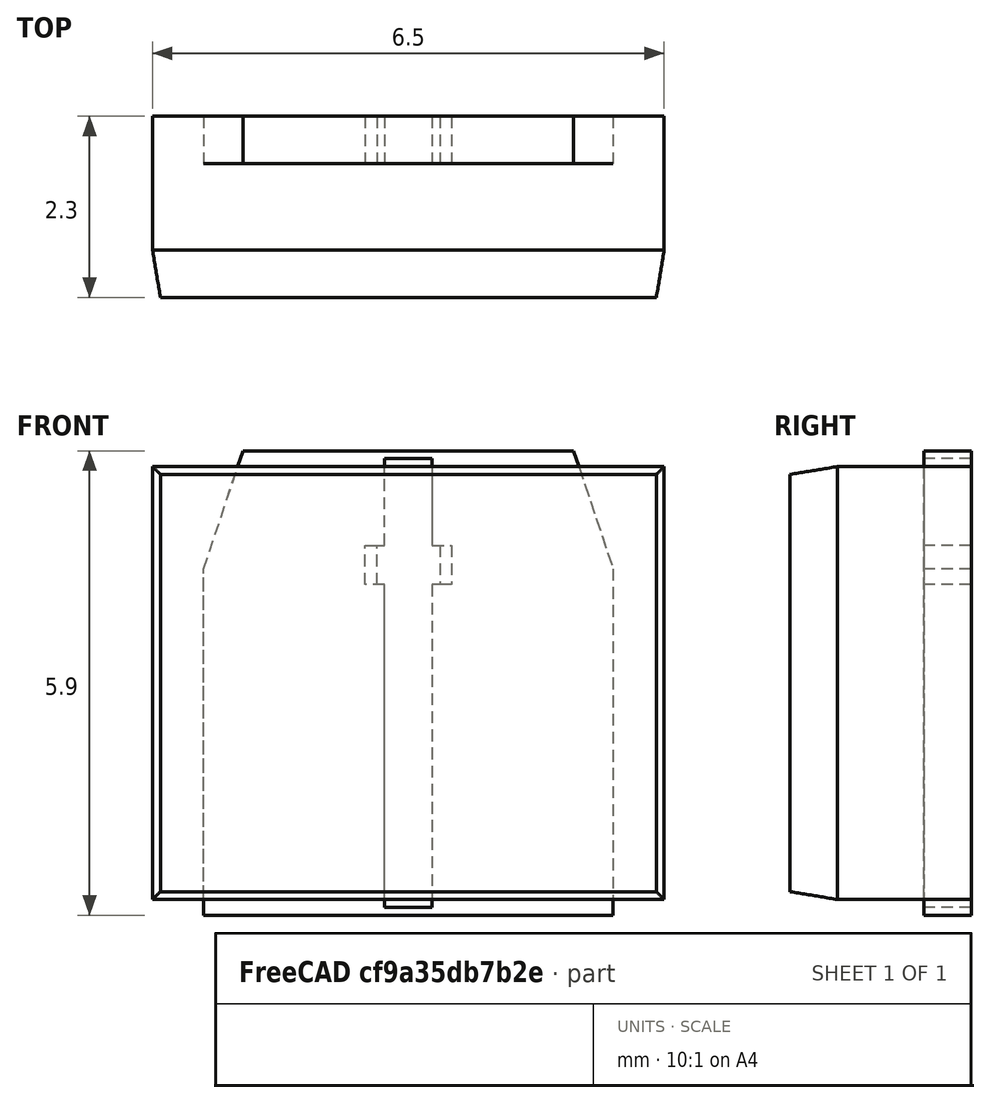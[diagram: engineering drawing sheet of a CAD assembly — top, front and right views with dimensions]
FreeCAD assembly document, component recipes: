
FREECAD ASSEMBLY — COMPONENT RECIPES ("2SK4017_3Dmodel")

This assembly document has 4 components, labeled P0..P3 below (a component is one placed body or linked part). 4 of them carry a construction recipe — the FreeCAD feature program that regenerates the part from scratch, quoted from this document or its linked companion documents; the rest are supplied as boundary geometry only. No exploded tour is included for this assembly.
COMPONENT P0 — recipe-attached ("樹脂体", modeled in this document).
Construction recipe (the document's own serialized feature program — sketch geometry with constraints, then the solid features built on it; lengths are millimeters unless a unit is written):

FEATURE [Sketcher::SketchObject] Sketch
  FullyConstrained = true
  MapMode = 5
  Placement = pos=(0,0,0) rot=(1,0,0;1.5708rad)
  Support = -> [XZ_Plane]
  sketch-geometry (4):
    g0: LineSegment StartX=-3.25 StartY=2.75 StartZ=0 EndX=3.25 EndY=2.75 EndZ=0
    g1: LineSegment StartX=3.25 StartY=2.75 StartZ=0 EndX=3.25 EndY=-2.75 EndZ=0
    g2: LineSegment StartX=3.25 StartY=-2.75 StartZ=0 EndX=-3.25 EndY=-2.75 EndZ=0
    g3: LineSegment StartX=-3.25 StartY=-2.75 StartZ=0 EndX=-3.25 EndY=2.75 EndZ=0
  constraints (11):
    c: Coincident(g0,g1)
    c: Coincident(g1,g2)
    c: Coincident(g2,g3)
    c: Coincident(g3,g0)
    c: Horizontal(g0)
    c: Horizontal(g2)
    c: Vertical(g1)
    c: Vertical(g3)
    c: DistanceX(g0,g0) = 6.5
    c: DistanceY(g1,g1) = 5.5
    c: Symmetric(g1,g0,g-1)
FEATURE [PartDesign::Pad] Pad
  Direction = (1,1,1)
  Length = 1.7
  Length2 = 100
  Placement = pos=(0,0,0) rot=(1,0,0;1.5708rad)
  Profile = -> Sketch
  Type = 0
FEATURE [Sketcher::SketchObject] Sketch001
  AttachmentOffset = pos=(0,0,0.6) rot=(0,0,1;0rad)
  FullyConstrained = true
  MapMode = 5
  Placement = pos=(0,-2.3,1e-15) rot=(1,0,0;1.5708rad)
  Support = -> [Pad]
  sketch-geometry (4):
    g0: LineSegment StartX=-3.15 StartY=2.65 StartZ=0 EndX=3.15 EndY=2.65 EndZ=0
    g1: LineSegment StartX=3.15 StartY=2.65 StartZ=0 EndX=3.15 EndY=-2.65 EndZ=0
    g2: LineSegment StartX=3.15 StartY=-2.65 StartZ=0 EndX=-3.15 EndY=-2.65 EndZ=0
    g3: LineSegment StartX=-3.15 StartY=-2.65 StartZ=0 EndX=-3.15 EndY=2.65 EndZ=0
  constraints (11):
    c: Coincident(g0,g1)
    c: Coincident(g1,g2)
    c: Coincident(g2,g3)
    c: Coincident(g3,g0)
    c: Horizontal(g0)
    c: Horizontal(g2)
    c: Vertical(g1)
    c: Vertical(g3)
    c: DistanceX(g0,g0) = 6.3
    c: DistanceY(g3,g3) = 5.3
    c: Symmetric(g1,g0,g-1)
FEATURE [Sketcher::SketchObject] Sketch002
  ExternalGeometry = -> [Pad]
  FullyConstrained = true
  MapMode = 5
  Placement = pos=(0,-1.7,8e-16) rot=(1,0,0;1.5708rad)
  Support = -> [Pad]
  sketch-geometry (4):
    g0: LineSegment StartX=-3.25 StartY=2.75 StartZ=0 EndX=3.25 EndY=2.75 EndZ=0
    g1: LineSegment StartX=3.25 StartY=2.75 StartZ=0 EndX=3.25 EndY=-2.75 EndZ=0
    g2: LineSegment StartX=3.25 StartY=-2.75 StartZ=0 EndX=-3.25 EndY=-2.75 EndZ=0
    g3: LineSegment StartX=-3.25 StartY=-2.75 StartZ=0 EndX=-3.25 EndY=2.75 EndZ=0
  constraints (10):
    c: Coincident(g0,g1)
    c: Coincident(g1,g2)
    c: Coincident(g2,g3)
    c: Coincident(g3,g0)
    c: Horizontal(g0)
    c: Horizontal(g2)
    c: Vertical(g1)
    c: Vertical(g3)
    c: Coincident(g1,g-4)
    c: Coincident(g-3,g0)
FEATURE [PartDesign::AdditiveLoft] AdditiveLoft
  BaseFeature = -> Pad
  Closed = false
  Placement = pos=(0,0,0) rot=(1,0,0;1.5708rad)
  Profile = -> Sketch001
  Ruled = false
  Sections = -> [Sketch002]
FEATURE [PartDesign::CoordinateSystem] ______  label="原点"
  AttacherType = Attacher::AttachEngine3D
  MapMode = 1
  Placement = pos=(-3.25,6e-16,2.75) rot=(0,0,1;0rad)
  Support = -> [Pad]
FEATURE [PartDesign::CoordinateSystem] _____________________  label="ドレインリード"
  AttacherType = Attacher::AttachEngine3D
  MapMode = 1
  Placement = pos=(-3.25,-1.7,-2.75) rot=(0,0,1;0rad)
  Support = -> [Pad]
FEATURE [PartDesign::CoordinateSystem] __________________001  label="ソースリード"
  AttacherType = Attacher::AttachEngine3D
  MapMode = 1
  Placement = pos=(-3.25,-1.7,-2.75) rot=(0,0,1;0rad)
  Support = -> [Pad]
FEATURE [PartDesign::CoordinateSystem] __________________002  label="ヒートシンク001"
  AttacherType = Attacher::AttachEngine3D
  AttachmentOffset = pos=(3.25,0,1.5) rot=(0,0,1;0rad)
  MapMode = 1
  Placement = pos=(0,6e-16,4.25) rot=(0,0,1;0rad)
  Support = -> [Pad]
FEATURE [PartDesign::Body] Body  label="樹脂体"
  Group = -> [Sketch,Pad,Sketch001,Sketch002,AdditiveLoft,______,_____________________,__________________001,__________________002]
  Origin = -> Origin
  Tip = -> AdditiveLoft
COMPONENT P1 — recipe-attached ("リードドレイン", modeled in this document).
Construction recipe (the document's own serialized feature program — sketch geometry with constraints, then the solid features built on it; lengths are millimeters unless a unit is written):

FEATURE [Sketcher::SketchObject] Sketch003
  FullyConstrained = true
  MapMode = 5
  Placement = pos=(0,0,0) rot=(1,0,0;1.5708rad)
  Support = -> [XZ_Plane001]
  sketch-geometry (12):
    g0: LineSegment StartX=-0.3 StartY=2.85 StartZ=0 EndX=0.3 EndY=2.85 EndZ=0
    g1: LineSegment StartX=0.3 StartY=2.85 StartZ=0 EndX=0.3 EndY=1.75 EndZ=0
    g2: LineSegment StartX=0.3 StartY=-2.85 StartZ=0 EndX=-0.3 EndY=-2.85 EndZ=0
    g3: LineSegment StartX=-0.3 StartY=-2.85 StartZ=0 EndX=-0.3 EndY=1.25 EndZ=0
    g4: LineSegment StartX=-0.55 StartY=1.75 StartZ=0 EndX=-0.3 EndY=1.75 EndZ=0
    g5: LineSegment StartX=0.55 StartY=1.75 StartZ=0 EndX=0.55 EndY=1.25 EndZ=0
    g6: LineSegment StartX=0.55 StartY=1.25 StartZ=0 EndX=0.3 EndY=1.25 EndZ=0
    g7: LineSegment StartX=-0.55 StartY=1.25 StartZ=0 EndX=-0.55 EndY=1.75 EndZ=0
    g8: LineSegment StartX=0.3 StartY=1.75 StartZ=0 EndX=0.55 EndY=1.75 EndZ=0
    g9: LineSegment StartX=0.3 StartY=1.25 StartZ=0 EndX=0.3 EndY=-2.85 EndZ=0
    g10: LineSegment StartX=-0.3 StartY=1.75 StartZ=0 EndX=-0.3 EndY=2.85 EndZ=0
    g11: LineSegment StartX=-0.3 StartY=1.25 StartZ=0 EndX=-0.55 EndY=1.25 EndZ=0
  constraints (30):
    c: Coincident(g0,g1)
    c: Coincident(g9,g2)
    c: Coincident(g2,g3)
    c: Coincident(g10,g0)
    c: Horizontal(g0)
    c: Horizontal(g2)
    c: Vertical(g1)
    c: Vertical(g3)
    c: Symmetric(g9,g0,g-1)
    c: DistanceX(g2,g2) = 0.6
    c: DistanceY(g9,g1) = 5.7
    c: Coincident(g8,g5)
    c: Coincident(g5,g6)
    c: Coincident(g11,g7)
    c: Coincident(g7,g4)
    c: Horizontal(g6)
    c: Vertical(g5)
    c: Vertical(g7)
    c: DistanceX(g11,g6) = 1.1
    c: DistanceY(g5,g5) = 0.5
    c: Symmetric(g8,g4,g-2)
    c: DistanceY(g9,g5) = 4.1
    c: Tangent(g4,g8)
    c: Coincident(g1,g8)
    c: Tangent(g1,g9)
    c: Coincident(g10,g4)
    c: Tangent(g3,g10)
    c: Coincident(g6,g9)
    c: Coincident(g11,g3)
    c: Tangent(g6,g11)
FEATURE [PartDesign::Pad] Pad001
  Direction = (1,1,1)
  Length = 0.6
  Length2 = 100
  Placement = pos=(0,0,0) rot=(1,0,0;1.5708rad)
  Profile = -> Sketch003
  Type = 0
FEATURE [PartDesign::CoordinateSystem] LCS_2
  AttacherType = Attacher::AttachEngine3D
  MapMode = 1
  Placement = pos=(-0.3,6e-16,2.85) rot=(0,0,1;0rad)
  Support = -> [Pad001]
FEATURE [PartDesign::Body] Body001  label="リードドレイン"
  Group = -> [Sketch003,Pad001,LCS_2]
  Origin = -> Origin001
  Tip = -> Pad001
COMPONENT P2 — recipe-attached ("リードゲートソース", modeled in this document).
Construction recipe (the document's own serialized feature program — sketch geometry with constraints, then the solid features built on it; lengths are millimeters unless a unit is written):

FEATURE [Sketcher::SketchObject] Sketch004
  FullyConstrained = true
  MapMode = 5
  Placement = pos=(0,0,0) rot=(1,0,0;1.5708rad)
  Support = -> [XZ_Plane002]
  sketch-geometry (12):
    g0: LineSegment StartX=-0.3 StartY=2.85 StartZ=0 EndX=0.3 EndY=2.85 EndZ=0
    g1: LineSegment StartX=0.3 StartY=2.85 StartZ=0 EndX=0.3 EndY=1.75 EndZ=0
    g2: LineSegment StartX=0.3 StartY=-2.85 StartZ=0 EndX=-0.3 EndY=-2.85 EndZ=0
    g3: LineSegment StartX=-0.3 StartY=-2.85 StartZ=0 EndX=-0.3 EndY=1.25 EndZ=0
    g4: LineSegment StartX=-0.4 StartY=1.75 StartZ=0 EndX=-0.3 EndY=1.75 EndZ=0
    g5: LineSegment StartX=0.4 StartY=1.75 StartZ=0 EndX=0.4 EndY=1.25 EndZ=0
    g6: LineSegment StartX=0.4 StartY=1.25 StartZ=0 EndX=0.3 EndY=1.25 EndZ=0
    g7: LineSegment StartX=-0.4 StartY=1.25 StartZ=0 EndX=-0.4 EndY=1.75 EndZ=0
    g8: LineSegment StartX=0.3 StartY=1.75 StartZ=0 EndX=0.4 EndY=1.75 EndZ=0
    g9: LineSegment StartX=0.3 StartY=1.25 StartZ=0 EndX=0.3 EndY=-2.85 EndZ=0
    g10: LineSegment StartX=-0.3 StartY=1.75 StartZ=0 EndX=-0.3 EndY=2.85 EndZ=0
    g11: LineSegment StartX=-0.3 StartY=1.25 StartZ=0 EndX=-0.4 EndY=1.25 EndZ=0
  constraints (30):
    c: Coincident(g0,g1)
    c: Coincident(g9,g2)
    c: Coincident(g2,g3)
    c: Coincident(g10,g0)
    c: Horizontal(g0)
    c: Horizontal(g2)
    c: Vertical(g1)
    c: Vertical(g3)
    c: DistanceY(g9,g1) = 5.7
    c: Symmetric(g9,g0,g-1)
    c: DistanceX(g0,g0) = 0.6
    c: Coincident(g8,g5)
    c: Coincident(g5,g6)
    c: Coincident(g11,g7)
    c: Coincident(g7,g4)
    c: Horizontal(g6)
    c: Vertical(g5)
    c: Vertical(g7)
    c: DistanceY(g7,g7) = 0.5
    c: DistanceY(g9,g5) = 4.1
    c: Symmetric(g8,g4,g-2)
    c: DistanceX(g4,g8) = 0.8
    c: Tangent(g4,g8)
    c: Coincident(g1,g8)
    c: Tangent(g1,g9)
    c: Coincident(g10,g4)
    c: Tangent(g3,g10)
    c: Coincident(g6,g9)
    c: Coincident(g11,g3)
    c: Tangent(g6,g11)
FEATURE [PartDesign::Pad] Pad002
  Direction = (1,1,1)
  Length = 0.6
  Length2 = 100
  Placement = pos=(0,0,0) rot=(1,0,0;1.5708rad)
  Profile = -> Sketch004
  Type = 0
FEATURE [PartDesign::CoordinateSystem] LCS_3
  AttacherType = Attacher::AttachEngine3D
  MapMode = 1
  Placement = pos=(-0.3,6e-16,2.85) rot=(0,0,1;0rad)
  Support = -> [Pad002]
FEATURE [PartDesign::Body] Body002  label="リードゲートソース"
  Group = -> [Sketch004,Pad002,LCS_3]
  Origin = -> Origin002
  Tip = -> Pad002
COMPONENT P3 — recipe-attached ("ヒートシンク", modeled in this document).
Construction recipe (the document's own serialized feature program — sketch geometry with constraints, then the solid features built on it; lengths are millimeters unless a unit is written):

FEATURE [Sketcher::SketchObject] Sketch005
  FullyConstrained = true
  MapMode = 5
  Placement = pos=(0,0,0) rot=(1,0,0;1.5708rad)
  Support = -> [XZ_Plane003]
  sketch-geometry (6):
    g0: LineSegment StartX=-2.6 StartY=-2.95 StartZ=0 EndX=-2.6 EndY=1.45 EndZ=0
    g1: LineSegment StartX=-2.6 StartY=1.45 StartZ=0 EndX=-2.1 EndY=2.95 EndZ=0
    g2: LineSegment StartX=-2.1 StartY=2.95 StartZ=0 EndX=2.1 EndY=2.95 EndZ=0
    g3: LineSegment StartX=2.1 StartY=2.95 StartZ=0 EndX=2.6 EndY=1.45 EndZ=0
    g4: LineSegment StartX=2.6 StartY=1.45 StartZ=0 EndX=2.6 EndY=-2.95 EndZ=0
    g5: LineSegment StartX=2.6 StartY=-2.95 StartZ=0 EndX=-2.6 EndY=-2.95 EndZ=0
  constraints (17):
    c: Vertical(g0)
    c: Coincident(g0,g1)
    c: Coincident(g1,g2)
    c: Coincident(g2,g3)
    c: Coincident(g3,g4)
    c: Vertical(g4)
    c: Coincident(g4,g5)
    c: Coincident(g5,g0)
    c: DistanceX(g2,g2) = 4.2
    c: DistanceY(g0,g0) = 4.4
    c: Horizontal(g0,g3)
    c: DistanceX(g5,g5) = 5.2
    c: Symmetric(g2,g1,g-2)
    c: Symmetric(g4,g0,g-2)
    c: DistanceY(g0,g1) = 1.5
    c: DistanceY(g4,g2) = 5.9
    c: DistanceY(g4,g-1) = 2.95
FEATURE [PartDesign::Pad] Pad003
  Direction = (1,1,1)
  Length = 0.6
  Length2 = 100
  Placement = pos=(0,0,0) rot=(1,0,0;1.5708rad)
  Profile = -> Sketch005
  Type = 0
FEATURE [PartDesign::CoordinateSystem] LCS_1
  AttacherType = Attacher::AttachEngine3D
  AttachmentOffset = pos=(2.6,0,1.5) rot=(0,0,1;0rad)
  MapMode = 1
  Placement = pos=(0,3e-16,2.95) rot=(0,0,1;0rad)
  Support = -> [Pad003]
FEATURE [PartDesign::Body] Body003  label="ヒートシンク"
  Group = -> [Sketch005,Pad003,LCS_1]
  Origin = -> Origin003
  Tip = -> Pad003
PROVENANCE & LICENSES
A FreeCAD (.FCStd) document from a public repository crawl; recipes are the document's own serialized feature recipes (and, for linked parts, companion documents' recipes).
License: as declared in the source repository (recorded in the dataset sidecar).
